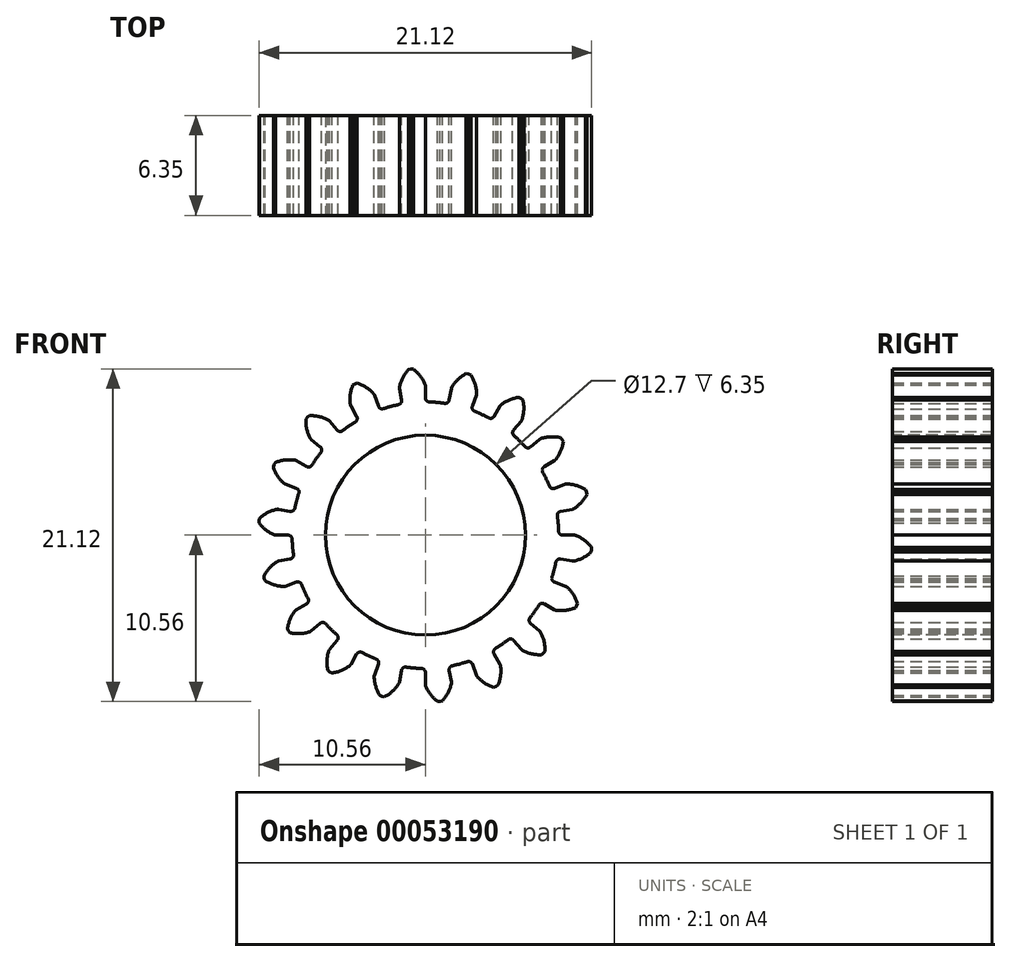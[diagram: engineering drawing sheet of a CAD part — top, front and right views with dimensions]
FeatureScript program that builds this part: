
annotation { "Feature Type Name" : "Feature", "Feature Type Description" : "" }
export const myFeature = defineFeature(function(context is Context, id is Id, definition is map)
    precondition{}
    {
        {
            var Q0;
            Q0=qCreatedBy(makeId("Front.planeOp"),FACE);
            var sketch = newSketch(context, id + "F0", { "sketchPlane" : qUnion([Q0])});
            skArc(sketch, "E0", {"start": v(-1.71, 8.3) * mm, "mid": v(-2.31, 8.15) * mm, "end": v(-2.9, 7.96) * mm});
            skLineSegment(sketch, "E1", {"start": v(0, 8.72) * mm, "end": v(0, 9.48) * mm});
            skArc(sketch, "E2", {"start": v(-0.02, 9.57) * mm, "mid": v(-0.33, 10.11) * mm, "end": v(-0.77, 10.56) * mm});
            skLineSegment(sketch, "E3", {"start": v(-0.77, 10.56) * mm, "end": v(-0.92, 10.56) * mm});
            skArc(sketch, "E4.MirrorCS", {"start": v(-1.64, 9.43) * mm, "mid": v(-1.43, 10.02) * mm, "end": v(-1.08, 10.53) * mm});
            skLineSegment(sketch, "E5.MirrorCS", {"start": v(-1.08, 10.53) * mm, "end": v(-0.92, 10.56) * mm});
            skLineSegment(sketch, "E6.MirrorCS", {"start": v(-1.51, 8.58) * mm, "end": v(-1.65, 9.33) * mm});
            skPoint(sketch, "E7.visualSharp", {"position": v(0, 9.53) * mm});
            skArc(sketch, "E7.filletArc", {"start": v(0, 9.48) * mm, "mid": v(0, 9.53) * mm, "end": v(-0.02, 9.57) * mm});
            skPoint(sketch, "E8.visualSharp", {"position": v(-1.65, 9.38) * mm});
            skArc(sketch, "E8.filletArc", {"start": v(-1.64, 9.43) * mm, "mid": v(-1.65, 9.38) * mm, "end": v(-1.65, 9.33) * mm});
            skPoint(sketch, "E9.visualSharp", {"position": v(0, 8.47) * mm});
            skArc(sketch, "E9.filletArc", {"start": v(0, 8.72) * mm, "mid": v(0.07, 8.54) * mm, "end": v(0.25, 8.46) * mm});
            skPoint(sketch, "E10.visualSharp", {"position": v(-1.47, 8.34) * mm});
            skArc(sketch, "E10.filletArc", {"start": v(-1.71, 8.3) * mm, "mid": v(-1.55, 8.4) * mm, "end": v(-1.51, 8.58) * mm});
            skLineSegment(sketch, "E11.1.0", {"start": v(-4.36, 7.55) * mm, "end": v(-4.74, 8.2) * mm});
            skLineSegment(sketch, "E11.1.1", {"start": v(-2.98, 8.2) * mm, "end": v(-3.24, 8.9) * mm});
            skPoint(sketch, "E11.1.2", {"position": v(-4.23, 7.33) * mm});
            skArc(sketch, "E11.1.3", {"start": v(-3.3, 8.99) * mm, "mid": v(-3.77, 9.4) * mm, "end": v(-4.33, 9.66) * mm});
            skArc(sketch, "E11.1.4", {"start": v(-2.98, 8.2) * mm, "mid": v(-2.85, 8.05) * mm, "end": v(-2.66, 8.04) * mm});
            skArc(sketch, "E11.1.5", {"start": v(-4.77, 8.3) * mm, "mid": v(-4.77, 8.92) * mm, "end": v(-4.61, 9.53) * mm});
            skPoint(sketch, "E11.1.6", {"position": v(-3.26, 8.95) * mm});
            skPoint(sketch, "E11.1.7", {"position": v(-4.76, 8.25) * mm});
            skPoint(sketch, "E11.1.8", {"position": v(-2.9, 7.96) * mm});
            skArc(sketch, "E11.1.9", {"start": v(-4.45, 7.2) * mm, "mid": v(-4.33, 7.36) * mm, "end": v(-4.36, 7.55) * mm});
            skLineSegment(sketch, "E11.1.10", {"start": v(-4.61, 9.53) * mm, "end": v(-4.48, 9.6) * mm});
            skLineSegment(sketch, "E11.1.11", {"start": v(-4.33, 9.66) * mm, "end": v(-4.48, 9.6) * mm});
            skArc(sketch, "E11.1.12", {"start": v(-4.77, 8.3) * mm, "mid": v(-4.76, 8.25) * mm, "end": v(-4.74, 8.2) * mm});
            skArc(sketch, "E11.1.13", {"start": v(-3.24, 8.9) * mm, "mid": v(-3.26, 8.95) * mm, "end": v(-3.3, 8.99) * mm});
            skLineSegment(sketch, "E11.2.0", {"start": v(-6.68, 5.6) * mm, "end": v(-7.26, 6.1) * mm});
            skLineSegment(sketch, "E11.2.1", {"start": v(-5.6, 6.68) * mm, "end": v(-6.1, 7.26) * mm});
            skPoint(sketch, "E11.2.2", {"position": v(-6.49, 5.44) * mm});
            skArc(sketch, "E11.2.3", {"start": v(-6.17, 7.32) * mm, "mid": v(-6.75, 7.54) * mm, "end": v(-7.37, 7.6) * mm});
            skArc(sketch, "E11.2.4", {"start": v(-5.6, 6.68) * mm, "mid": v(-5.43, 6.59) * mm, "end": v(-5.25, 6.64) * mm});
            skArc(sketch, "E11.2.5", {"start": v(-7.32, 6.17) * mm, "mid": v(-7.54, 6.75) * mm, "end": v(-7.6, 7.37) * mm});
            skPoint(sketch, "E11.2.6", {"position": v(-6.12, 7.3) * mm});
            skPoint(sketch, "E11.2.7", {"position": v(-7.3, 6.12) * mm});
            skPoint(sketch, "E11.2.8", {"position": v(-5.44, 6.49) * mm});
            skArc(sketch, "E11.2.9", {"start": v(-6.64, 5.25) * mm, "mid": v(-6.59, 5.43) * mm, "end": v(-6.68, 5.6) * mm});
            skLineSegment(sketch, "E11.2.10", {"start": v(-7.6, 7.37) * mm, "end": v(-7.5, 7.5) * mm});
            skLineSegment(sketch, "E11.2.11", {"start": v(-7.37, 7.6) * mm, "end": v(-7.5, 7.5) * mm});
            skArc(sketch, "E11.2.12", {"start": v(-7.32, 6.17) * mm, "mid": v(-7.3, 6.13) * mm, "end": v(-7.26, 6.1) * mm});
            skArc(sketch, "E11.2.13", {"start": v(-6.1, 7.26) * mm, "mid": v(-6.13, 7.3) * mm, "end": v(-6.17, 7.32) * mm});
            skLineSegment(sketch, "E11.3.0", {"start": v(-8.2, 2.98) * mm, "end": v(-8.9, 3.24) * mm});
            skLineSegment(sketch, "E11.3.1", {"start": v(-7.55, 4.36) * mm, "end": v(-8.2, 4.74) * mm});
            skPoint(sketch, "E11.3.2", {"position": v(-7.96, 2.9) * mm});
            skArc(sketch, "E11.3.3", {"start": v(-8.3, 4.77) * mm, "mid": v(-8.92, 4.77) * mm, "end": v(-9.53, 4.61) * mm});
            skArc(sketch, "E11.3.4", {"start": v(-7.55, 4.36) * mm, "mid": v(-7.36, 4.33) * mm, "end": v(-7.2, 4.45) * mm});
            skArc(sketch, "E11.3.5", {"start": v(-8.99, 3.3) * mm, "mid": v(-9.4, 3.77) * mm, "end": v(-9.66, 4.33) * mm});
            skPoint(sketch, "E11.3.6", {"position": v(-8.25, 4.76) * mm});
            skPoint(sketch, "E11.3.7", {"position": v(-8.95, 3.26) * mm});
            skPoint(sketch, "E11.3.8", {"position": v(-7.33, 4.23) * mm});
            skArc(sketch, "E11.3.9", {"start": v(-8.04, 2.66) * mm, "mid": v(-8.05, 2.85) * mm, "end": v(-8.2, 2.98) * mm});
            skLineSegment(sketch, "E11.3.10", {"start": v(-9.66, 4.33) * mm, "end": v(-9.6, 4.48) * mm});
            skLineSegment(sketch, "E11.3.11", {"start": v(-9.53, 4.61) * mm, "end": v(-9.6, 4.48) * mm});
            skArc(sketch, "E11.3.12", {"start": v(-8.99, 3.3) * mm, "mid": v(-8.95, 3.26) * mm, "end": v(-8.9, 3.24) * mm});
            skArc(sketch, "E11.3.13", {"start": v(-8.2, 4.74) * mm, "mid": v(-8.25, 4.76) * mm, "end": v(-8.3, 4.77) * mm});
            skLineSegment(sketch, "E11.4.0", {"start": v(-8.72, 0) * mm, "end": v(-9.48, 0) * mm});
            skLineSegment(sketch, "E11.4.1", {"start": v(-8.58, 1.51) * mm, "end": v(-9.33, 1.65) * mm});
            skPoint(sketch, "E11.4.2", {"position": v(-8.47, 0) * mm});
            skArc(sketch, "E11.4.3", {"start": v(-9.43, 1.64) * mm, "mid": v(-10.02, 1.43) * mm, "end": v(-10.53, 1.08) * mm});
            skArc(sketch, "E11.4.4", {"start": v(-8.58, 1.51) * mm, "mid": v(-8.4, 1.55) * mm, "end": v(-8.3, 1.71) * mm});
            skArc(sketch, "E11.4.5", {"start": v(-9.57, 0.02) * mm, "mid": v(-10.11, 0.33) * mm, "end": v(-10.56, 0.77) * mm});
            skPoint(sketch, "E11.4.6", {"position": v(-9.38, 1.65) * mm});
            skPoint(sketch, "E11.4.7", {"position": v(-9.53, 0) * mm});
            skPoint(sketch, "E11.4.8", {"position": v(-8.34, 1.47) * mm});
            skArc(sketch, "E11.4.9", {"start": v(-8.46, -0.25) * mm, "mid": v(-8.54, -0.07) * mm, "end": v(-8.72, 0) * mm});
            skLineSegment(sketch, "E11.4.10", {"start": v(-10.56, 0.77) * mm, "end": v(-10.56, 0.92) * mm});
            skLineSegment(sketch, "E11.4.11", {"start": v(-10.53, 1.08) * mm, "end": v(-10.56, 0.92) * mm});
            skArc(sketch, "E11.4.12", {"start": v(-9.57, 0.02) * mm, "mid": v(-9.53, 0) * mm, "end": v(-9.48, 0) * mm});
            skArc(sketch, "E11.4.13", {"start": v(-9.33, 1.65) * mm, "mid": v(-9.38, 1.65) * mm, "end": v(-9.43, 1.64) * mm});
            skLineSegment(sketch, "E11.5.0", {"start": v(-8.2, -2.98) * mm, "end": v(-8.9, -3.24) * mm});
            skLineSegment(sketch, "E11.5.1", {"start": v(-8.58, -1.51) * mm, "end": v(-9.33, -1.65) * mm});
            skPoint(sketch, "E11.5.2", {"position": v(-7.96, -2.9) * mm});
            skArc(sketch, "E11.5.3", {"start": v(-9.42, -1.68) * mm, "mid": v(-9.9, -2.08) * mm, "end": v(-10.26, -2.59) * mm});
            skArc(sketch, "E11.5.4", {"start": v(-8.58, -1.51) * mm, "mid": v(-8.42, -1.41) * mm, "end": v(-8.38, -1.23) * mm});
            skArc(sketch, "E11.5.5", {"start": v(-9, -3.26) * mm, "mid": v(-9.62, -3.15) * mm, "end": v(-10.18, -2.89) * mm});
            skPoint(sketch, "E11.5.6", {"position": v(-9.38, -1.65) * mm});
            skPoint(sketch, "E11.5.7", {"position": v(-8.95, -3.26) * mm});
            skPoint(sketch, "E11.5.8", {"position": v(-8.34, -1.47) * mm});
            skArc(sketch, "E11.5.9", {"start": v(-7.87, -3.13) * mm, "mid": v(-8, -2.99) * mm, "end": v(-8.2, -2.98) * mm});
            skLineSegment(sketch, "E11.5.10", {"start": v(-10.18, -2.89) * mm, "end": v(-10.23, -2.74) * mm});
            skLineSegment(sketch, "E11.5.11", {"start": v(-10.26, -2.59) * mm, "end": v(-10.23, -2.74) * mm});
            skArc(sketch, "E11.5.12", {"start": v(-9, -3.26) * mm, "mid": v(-8.95, -3.25) * mm, "end": v(-8.9, -3.24) * mm});
            skArc(sketch, "E11.5.13", {"start": v(-9.33, -1.65) * mm, "mid": v(-9.38, -1.66) * mm, "end": v(-9.42, -1.68) * mm});
            skLineSegment(sketch, "E11.6.0", {"start": v(-6.68, -5.6) * mm, "end": v(-7.26, -6.1) * mm});
            skLineSegment(sketch, "E11.6.1", {"start": v(-7.55, -4.36) * mm, "end": v(-8.2, -4.74) * mm});
            skPoint(sketch, "E11.6.2", {"position": v(-6.49, -5.44) * mm});
            skArc(sketch, "E11.6.3", {"start": v(-8.28, -4.8) * mm, "mid": v(-8.6, -5.34) * mm, "end": v(-8.76, -5.94) * mm});
            skArc(sketch, "E11.6.4", {"start": v(-7.55, -4.36) * mm, "mid": v(-7.43, -4.2) * mm, "end": v(-7.45, -4.02) * mm});
            skArc(sketch, "E11.6.5", {"start": v(-7.35, -6.14) * mm, "mid": v(-7.96, -6.25) * mm, "end": v(-8.58, -6.2) * mm});
            skPoint(sketch, "E11.6.6", {"position": v(-8.25, -4.76) * mm});
            skPoint(sketch, "E11.6.7", {"position": v(-7.3, -6.12) * mm});
            skPoint(sketch, "E11.6.8", {"position": v(-7.33, -4.23) * mm});
            skArc(sketch, "E11.6.9", {"start": v(-6.32, -5.63) * mm, "mid": v(-6.5, -5.54) * mm, "end": v(-6.68, -5.6) * mm});
            skLineSegment(sketch, "E11.6.10", {"start": v(-8.58, -6.2) * mm, "end": v(-8.68, -6.08) * mm});
            skLineSegment(sketch, "E11.6.11", {"start": v(-8.76, -5.94) * mm, "end": v(-8.68, -6.08) * mm});
            skArc(sketch, "E11.6.12", {"start": v(-7.35, -6.14) * mm, "mid": v(-7.3, -6.12) * mm, "end": v(-7.26, -6.1) * mm});
            skArc(sketch, "E11.6.13", {"start": v(-8.2, -4.74) * mm, "mid": v(-8.25, -4.77) * mm, "end": v(-8.28, -4.8) * mm});
            skLineSegment(sketch, "E11.7.0", {"start": v(-4.36, -7.55) * mm, "end": v(-4.74, -8.2) * mm});
            skLineSegment(sketch, "E11.7.1", {"start": v(-5.6, -6.68) * mm, "end": v(-6.1, -7.26) * mm});
            skPoint(sketch, "E11.7.2", {"position": v(-4.23, -7.33) * mm});
            skArc(sketch, "E11.7.3", {"start": v(-6.14, -7.35) * mm, "mid": v(-6.25, -7.96) * mm, "end": v(-6.2, -8.58) * mm});
            skArc(sketch, "E11.7.4", {"start": v(-5.6, -6.68) * mm, "mid": v(-5.54, -6.5) * mm, "end": v(-5.63, -6.32) * mm});
            skArc(sketch, "E11.7.5", {"start": v(-4.8, -8.28) * mm, "mid": v(-5.34, -8.6) * mm, "end": v(-5.94, -8.76) * mm});
            skPoint(sketch, "E11.7.6", {"position": v(-6.12, -7.3) * mm});
            skPoint(sketch, "E11.7.7", {"position": v(-4.76, -8.25) * mm});
            skPoint(sketch, "E11.7.8", {"position": v(-5.44, -6.49) * mm});
            skArc(sketch, "E11.7.9", {"start": v(-4.02, -7.45) * mm, "mid": v(-4.2, -7.43) * mm, "end": v(-4.36, -7.55) * mm});
            skLineSegment(sketch, "E11.7.10", {"start": v(-5.94, -8.76) * mm, "end": v(-6.08, -8.68) * mm});
            skLineSegment(sketch, "E11.7.11", {"start": v(-6.2, -8.58) * mm, "end": v(-6.08, -8.68) * mm});
            skArc(sketch, "E11.7.12", {"start": v(-4.8, -8.28) * mm, "mid": v(-4.77, -8.25) * mm, "end": v(-4.74, -8.2) * mm});
            skArc(sketch, "E11.7.13", {"start": v(-6.1, -7.26) * mm, "mid": v(-6.12, -7.3) * mm, "end": v(-6.14, -7.35) * mm});
            skLineSegment(sketch, "E11.8.0", {"start": v(-1.51, -8.58) * mm, "end": v(-1.65, -9.33) * mm});
            skLineSegment(sketch, "E11.8.1", {"start": v(-2.98, -8.2) * mm, "end": v(-3.24, -8.9) * mm});
            skPoint(sketch, "E11.8.2", {"position": v(-1.47, -8.34) * mm});
            skArc(sketch, "E11.8.3", {"start": v(-3.26, -9) * mm, "mid": v(-3.15, -9.62) * mm, "end": v(-2.89, -10.18) * mm});
            skArc(sketch, "E11.8.4", {"start": v(-2.98, -8.2) * mm, "mid": v(-2.99, -8) * mm, "end": v(-3.13, -7.87) * mm});
            skArc(sketch, "E11.8.5", {"start": v(-1.68, -9.42) * mm, "mid": v(-2.08, -9.9) * mm, "end": v(-2.59, -10.26) * mm});
            skPoint(sketch, "E11.8.6", {"position": v(-3.26, -8.95) * mm});
            skPoint(sketch, "E11.8.7", {"position": v(-1.65, -9.38) * mm});
            skPoint(sketch, "E11.8.8", {"position": v(-2.9, -7.96) * mm});
            skArc(sketch, "E11.8.9", {"start": v(-1.23, -8.38) * mm, "mid": v(-1.41, -8.42) * mm, "end": v(-1.51, -8.58) * mm});
            skLineSegment(sketch, "E11.8.10", {"start": v(-2.59, -10.26) * mm, "end": v(-2.74, -10.23) * mm});
            skLineSegment(sketch, "E11.8.11", {"start": v(-2.89, -10.18) * mm, "end": v(-2.74, -10.23) * mm});
            skArc(sketch, "E11.8.12", {"start": v(-1.68, -9.42) * mm, "mid": v(-1.66, -9.38) * mm, "end": v(-1.65, -9.33) * mm});
            skArc(sketch, "E11.8.13", {"start": v(-3.24, -8.9) * mm, "mid": v(-3.25, -8.95) * mm, "end": v(-3.26, -9) * mm});
            skLineSegment(sketch, "E11.9.0", {"start": v(1.51, -8.58) * mm, "end": v(1.65, -9.33) * mm});
            skLineSegment(sketch, "E11.9.1", {"start": v(0, -8.72) * mm, "end": v(0, -9.48) * mm});
            skPoint(sketch, "E11.9.2", {"position": v(1.47, -8.34) * mm});
            skArc(sketch, "E11.9.3", {"start": v(0.02, -9.57) * mm, "mid": v(0.33, -10.11) * mm, "end": v(0.77, -10.56) * mm});
            skArc(sketch, "E11.9.4", {"start": v(0, -8.72) * mm, "mid": v(-0.07, -8.54) * mm, "end": v(-0.25, -8.46) * mm});
            skArc(sketch, "E11.9.5", {"start": v(1.64, -9.43) * mm, "mid": v(1.43, -10.02) * mm, "end": v(1.08, -10.53) * mm});
            skPoint(sketch, "E11.9.6", {"position": v(0, -9.53) * mm});
            skPoint(sketch, "E11.9.7", {"position": v(1.65, -9.38) * mm});
            skPoint(sketch, "E11.9.8", {"position": v(0, -8.47) * mm});
            skArc(sketch, "E11.9.9", {"start": v(1.71, -8.3) * mm, "mid": v(1.55, -8.4) * mm, "end": v(1.51, -8.58) * mm});
            skLineSegment(sketch, "E11.9.10", {"start": v(1.08, -10.53) * mm, "end": v(0.92, -10.56) * mm});
            skLineSegment(sketch, "E11.9.11", {"start": v(0.77, -10.56) * mm, "end": v(0.92, -10.56) * mm});
            skArc(sketch, "E11.9.12", {"start": v(1.64, -9.43) * mm, "mid": v(1.65, -9.38) * mm, "end": v(1.65, -9.33) * mm});
            skArc(sketch, "E11.9.13", {"start": v(0, -9.48) * mm, "mid": v(0, -9.53) * mm, "end": v(0.02, -9.57) * mm});
            skLineSegment(sketch, "E11.10.0", {"start": v(4.36, -7.55) * mm, "end": v(4.74, -8.2) * mm});
            skLineSegment(sketch, "E11.10.1", {"start": v(2.98, -8.2) * mm, "end": v(3.24, -8.9) * mm});
            skPoint(sketch, "E11.10.2", {"position": v(4.23, -7.33) * mm});
            skArc(sketch, "E11.10.3", {"start": v(3.3, -8.99) * mm, "mid": v(3.77, -9.4) * mm, "end": v(4.33, -9.66) * mm});
            skArc(sketch, "E11.10.4", {"start": v(2.98, -8.2) * mm, "mid": v(2.85, -8.05) * mm, "end": v(2.66, -8.04) * mm});
            skArc(sketch, "E11.10.5", {"start": v(4.77, -8.3) * mm, "mid": v(4.77, -8.92) * mm, "end": v(4.61, -9.53) * mm});
            skPoint(sketch, "E11.10.6", {"position": v(3.26, -8.95) * mm});
            skPoint(sketch, "E11.10.7", {"position": v(4.76, -8.25) * mm});
            skPoint(sketch, "E11.10.8", {"position": v(2.9, -7.96) * mm});
            skArc(sketch, "E11.10.9", {"start": v(4.45, -7.2) * mm, "mid": v(4.33, -7.36) * mm, "end": v(4.36, -7.55) * mm});
            skLineSegment(sketch, "E11.10.10", {"start": v(4.61, -9.53) * mm, "end": v(4.48, -9.6) * mm});
            skLineSegment(sketch, "E11.10.11", {"start": v(4.33, -9.66) * mm, "end": v(4.48, -9.6) * mm});
            skArc(sketch, "E11.10.12", {"start": v(4.77, -8.3) * mm, "mid": v(4.76, -8.25) * mm, "end": v(4.74, -8.2) * mm});
            skArc(sketch, "E11.10.13", {"start": v(3.24, -8.9) * mm, "mid": v(3.26, -8.95) * mm, "end": v(3.3, -8.99) * mm});
            skLineSegment(sketch, "E11.11.0", {"start": v(6.68, -5.6) * mm, "end": v(7.26, -6.1) * mm});
            skLineSegment(sketch, "E11.11.1", {"start": v(5.6, -6.68) * mm, "end": v(6.1, -7.26) * mm});
            skPoint(sketch, "E11.11.2", {"position": v(6.49, -5.44) * mm});
            skArc(sketch, "E11.11.3", {"start": v(6.17, -7.32) * mm, "mid": v(6.75, -7.54) * mm, "end": v(7.37, -7.6) * mm});
            skArc(sketch, "E11.11.4", {"start": v(5.6, -6.68) * mm, "mid": v(5.43, -6.59) * mm, "end": v(5.25, -6.64) * mm});
            skArc(sketch, "E11.11.5", {"start": v(7.32, -6.17) * mm, "mid": v(7.54, -6.75) * mm, "end": v(7.6, -7.37) * mm});
            skPoint(sketch, "E11.11.6", {"position": v(6.12, -7.3) * mm});
            skPoint(sketch, "E11.11.7", {"position": v(7.3, -6.12) * mm});
            skPoint(sketch, "E11.11.8", {"position": v(5.44, -6.49) * mm});
            skArc(sketch, "E11.11.9", {"start": v(6.64, -5.25) * mm, "mid": v(6.59, -5.43) * mm, "end": v(6.68, -5.6) * mm});
            skLineSegment(sketch, "E11.11.10", {"start": v(7.6, -7.37) * mm, "end": v(7.5, -7.5) * mm});
            skLineSegment(sketch, "E11.11.11", {"start": v(7.37, -7.6) * mm, "end": v(7.5, -7.5) * mm});
            skArc(sketch, "E11.11.12", {"start": v(7.32, -6.17) * mm, "mid": v(7.3, -6.13) * mm, "end": v(7.26, -6.1) * mm});
            skArc(sketch, "E11.11.13", {"start": v(6.1, -7.26) * mm, "mid": v(6.13, -7.3) * mm, "end": v(6.17, -7.32) * mm});
            skLineSegment(sketch, "E11.12.0", {"start": v(8.2, -2.98) * mm, "end": v(8.9, -3.24) * mm});
            skLineSegment(sketch, "E11.12.1", {"start": v(7.55, -4.36) * mm, "end": v(8.2, -4.74) * mm});
            skPoint(sketch, "E11.12.2", {"position": v(7.96, -2.9) * mm});
            skArc(sketch, "E11.12.3", {"start": v(8.3, -4.77) * mm, "mid": v(8.92, -4.77) * mm, "end": v(9.53, -4.61) * mm});
            skArc(sketch, "E11.12.4", {"start": v(7.55, -4.36) * mm, "mid": v(7.36, -4.33) * mm, "end": v(7.2, -4.45) * mm});
            skArc(sketch, "E11.12.5", {"start": v(8.99, -3.3) * mm, "mid": v(9.4, -3.77) * mm, "end": v(9.66, -4.33) * mm});
            skPoint(sketch, "E11.12.6", {"position": v(8.25, -4.76) * mm});
            skPoint(sketch, "E11.12.7", {"position": v(8.95, -3.26) * mm});
            skPoint(sketch, "E11.12.8", {"position": v(7.33, -4.23) * mm});
            skArc(sketch, "E11.12.9", {"start": v(8.04, -2.66) * mm, "mid": v(8.05, -2.85) * mm, "end": v(8.2, -2.98) * mm});
            skLineSegment(sketch, "E11.12.10", {"start": v(9.66, -4.33) * mm, "end": v(9.6, -4.48) * mm});
            skLineSegment(sketch, "E11.12.11", {"start": v(9.53, -4.61) * mm, "end": v(9.6, -4.48) * mm});
            skArc(sketch, "E11.12.12", {"start": v(8.99, -3.3) * mm, "mid": v(8.95, -3.26) * mm, "end": v(8.9, -3.24) * mm});
            skArc(sketch, "E11.12.13", {"start": v(8.2, -4.74) * mm, "mid": v(8.25, -4.76) * mm, "end": v(8.3, -4.77) * mm});
            skLineSegment(sketch, "E11.13.0", {"start": v(8.72, 0) * mm, "end": v(9.48, 0) * mm});
            skLineSegment(sketch, "E11.13.1", {"start": v(8.58, -1.51) * mm, "end": v(9.33, -1.65) * mm});
            skPoint(sketch, "E11.13.2", {"position": v(8.47, 0) * mm});
            skArc(sketch, "E11.13.3", {"start": v(9.43, -1.64) * mm, "mid": v(10.02, -1.43) * mm, "end": v(10.53, -1.08) * mm});
            skArc(sketch, "E11.13.4", {"start": v(8.58, -1.51) * mm, "mid": v(8.4, -1.55) * mm, "end": v(8.3, -1.71) * mm});
            skArc(sketch, "E11.13.5", {"start": v(9.57, -0.02) * mm, "mid": v(10.11, -0.33) * mm, "end": v(10.56, -0.77) * mm});
            skPoint(sketch, "E11.13.6", {"position": v(9.38, -1.65) * mm});
            skPoint(sketch, "E11.13.7", {"position": v(9.53, 0) * mm});
            skPoint(sketch, "E11.13.8", {"position": v(8.34, -1.47) * mm});
            skArc(sketch, "E11.13.9", {"start": v(8.46, 0.25) * mm, "mid": v(8.54, 0.07) * mm, "end": v(8.72, 0) * mm});
            skLineSegment(sketch, "E11.13.10", {"start": v(10.56, -0.77) * mm, "end": v(10.56, -0.92) * mm});
            skLineSegment(sketch, "E11.13.11", {"start": v(10.53, -1.08) * mm, "end": v(10.56, -0.92) * mm});
            skArc(sketch, "E11.13.12", {"start": v(9.57, -0.02) * mm, "mid": v(9.53, 0) * mm, "end": v(9.48, 0) * mm});
            skArc(sketch, "E11.13.13", {"start": v(9.33, -1.65) * mm, "mid": v(9.38, -1.65) * mm, "end": v(9.43, -1.64) * mm});
            skLineSegment(sketch, "E11.14.0", {"start": v(8.2, 2.98) * mm, "end": v(8.9, 3.24) * mm});
            skLineSegment(sketch, "E11.14.1", {"start": v(8.58, 1.51) * mm, "end": v(9.33, 1.65) * mm});
            skPoint(sketch, "E11.14.2", {"position": v(7.96, 2.9) * mm});
            skArc(sketch, "E11.14.3", {"start": v(9.42, 1.68) * mm, "mid": v(9.9, 2.08) * mm, "end": v(10.26, 2.59) * mm});
            skArc(sketch, "E11.14.4", {"start": v(8.58, 1.51) * mm, "mid": v(8.42, 1.41) * mm, "end": v(8.38, 1.23) * mm});
            skArc(sketch, "E11.14.5", {"start": v(9, 3.26) * mm, "mid": v(9.62, 3.15) * mm, "end": v(10.18, 2.89) * mm});
            skPoint(sketch, "E11.14.6", {"position": v(9.38, 1.65) * mm});
            skPoint(sketch, "E11.14.7", {"position": v(8.95, 3.26) * mm});
            skPoint(sketch, "E11.14.8", {"position": v(8.34, 1.47) * mm});
            skArc(sketch, "E11.14.9", {"start": v(7.87, 3.13) * mm, "mid": v(8, 2.99) * mm, "end": v(8.2, 2.98) * mm});
            skLineSegment(sketch, "E11.14.10", {"start": v(10.18, 2.89) * mm, "end": v(10.23, 2.74) * mm});
            skLineSegment(sketch, "E11.14.11", {"start": v(10.26, 2.59) * mm, "end": v(10.23, 2.74) * mm});
            skArc(sketch, "E11.14.12", {"start": v(9, 3.26) * mm, "mid": v(8.95, 3.25) * mm, "end": v(8.9, 3.24) * mm});
            skArc(sketch, "E11.14.13", {"start": v(9.33, 1.65) * mm, "mid": v(9.38, 1.66) * mm, "end": v(9.42, 1.68) * mm});
            skLineSegment(sketch, "E11.15.0", {"start": v(6.68, 5.6) * mm, "end": v(7.26, 6.1) * mm});
            skLineSegment(sketch, "E11.15.1", {"start": v(7.55, 4.36) * mm, "end": v(8.2, 4.74) * mm});
            skPoint(sketch, "E11.15.2", {"position": v(6.49, 5.44) * mm});
            skArc(sketch, "E11.15.3", {"start": v(8.28, 4.8) * mm, "mid": v(8.6, 5.34) * mm, "end": v(8.76, 5.94) * mm});
            skArc(sketch, "E11.15.4", {"start": v(7.55, 4.36) * mm, "mid": v(7.43, 4.2) * mm, "end": v(7.45, 4.02) * mm});
            skArc(sketch, "E11.15.5", {"start": v(7.35, 6.14) * mm, "mid": v(7.96, 6.25) * mm, "end": v(8.58, 6.2) * mm});
            skPoint(sketch, "E11.15.6", {"position": v(8.25, 4.76) * mm});
            skPoint(sketch, "E11.15.7", {"position": v(7.3, 6.12) * mm});
            skPoint(sketch, "E11.15.8", {"position": v(7.33, 4.23) * mm});
            skArc(sketch, "E11.15.9", {"start": v(6.32, 5.63) * mm, "mid": v(6.5, 5.54) * mm, "end": v(6.68, 5.6) * mm});
            skLineSegment(sketch, "E11.15.10", {"start": v(8.58, 6.2) * mm, "end": v(8.68, 6.08) * mm});
            skLineSegment(sketch, "E11.15.11", {"start": v(8.76, 5.94) * mm, "end": v(8.68, 6.08) * mm});
            skArc(sketch, "E11.15.12", {"start": v(7.35, 6.14) * mm, "mid": v(7.3, 6.12) * mm, "end": v(7.26, 6.1) * mm});
            skArc(sketch, "E11.15.13", {"start": v(8.2, 4.74) * mm, "mid": v(8.25, 4.77) * mm, "end": v(8.28, 4.8) * mm});
            skLineSegment(sketch, "E11.16.0", {"start": v(4.36, 7.55) * mm, "end": v(4.74, 8.2) * mm});
            skLineSegment(sketch, "E11.16.1", {"start": v(5.6, 6.68) * mm, "end": v(6.1, 7.26) * mm});
            skPoint(sketch, "E11.16.2", {"position": v(4.23, 7.33) * mm});
            skArc(sketch, "E11.16.3", {"start": v(6.14, 7.35) * mm, "mid": v(6.25, 7.96) * mm, "end": v(6.2, 8.58) * mm});
            skArc(sketch, "E11.16.4", {"start": v(5.6, 6.68) * mm, "mid": v(5.54, 6.5) * mm, "end": v(5.63, 6.32) * mm});
            skArc(sketch, "E11.16.5", {"start": v(4.8, 8.28) * mm, "mid": v(5.34, 8.6) * mm, "end": v(5.94, 8.76) * mm});
            skPoint(sketch, "E11.16.6", {"position": v(6.12, 7.3) * mm});
            skPoint(sketch, "E11.16.7", {"position": v(4.76, 8.25) * mm});
            skPoint(sketch, "E11.16.8", {"position": v(5.44, 6.49) * mm});
            skArc(sketch, "E11.16.9", {"start": v(4.02, 7.45) * mm, "mid": v(4.2, 7.43) * mm, "end": v(4.36, 7.55) * mm});
            skLineSegment(sketch, "E11.16.10", {"start": v(5.94, 8.76) * mm, "end": v(6.08, 8.68) * mm});
            skLineSegment(sketch, "E11.16.11", {"start": v(6.2, 8.58) * mm, "end": v(6.08, 8.68) * mm});
            skArc(sketch, "E11.16.12", {"start": v(4.8, 8.28) * mm, "mid": v(4.77, 8.25) * mm, "end": v(4.74, 8.2) * mm});
            skArc(sketch, "E11.16.13", {"start": v(6.1, 7.26) * mm, "mid": v(6.12, 7.3) * mm, "end": v(6.14, 7.35) * mm});
            skLineSegment(sketch, "E11.17.0", {"start": v(1.51, 8.58) * mm, "end": v(1.65, 9.33) * mm});
            skLineSegment(sketch, "E11.17.1", {"start": v(2.98, 8.2) * mm, "end": v(3.24, 8.9) * mm});
            skPoint(sketch, "E11.17.2", {"position": v(1.47, 8.34) * mm});
            skArc(sketch, "E11.17.3", {"start": v(3.26, 9) * mm, "mid": v(3.15, 9.62) * mm, "end": v(2.89, 10.18) * mm});
            skArc(sketch, "E11.17.4", {"start": v(2.98, 8.2) * mm, "mid": v(2.99, 8) * mm, "end": v(3.13, 7.87) * mm});
            skArc(sketch, "E11.17.5", {"start": v(1.68, 9.42) * mm, "mid": v(2.08, 9.9) * mm, "end": v(2.59, 10.26) * mm});
            skPoint(sketch, "E11.17.6", {"position": v(3.26, 8.95) * mm});
            skPoint(sketch, "E11.17.7", {"position": v(1.65, 9.38) * mm});
            skPoint(sketch, "E11.17.8", {"position": v(2.9, 7.96) * mm});
            skArc(sketch, "E11.17.9", {"start": v(1.23, 8.38) * mm, "mid": v(1.41, 8.42) * mm, "end": v(1.51, 8.58) * mm});
            skLineSegment(sketch, "E11.17.10", {"start": v(2.59, 10.26) * mm, "end": v(2.74, 10.23) * mm});
            skLineSegment(sketch, "E11.17.11", {"start": v(2.89, 10.18) * mm, "end": v(2.74, 10.23) * mm});
            skArc(sketch, "E11.17.12", {"start": v(1.68, 9.42) * mm, "mid": v(1.66, 9.38) * mm, "end": v(1.65, 9.33) * mm});
            skArc(sketch, "E11.17.13", {"start": v(3.24, 8.9) * mm, "mid": v(3.25, 8.95) * mm, "end": v(3.26, 9) * mm});
            skArc(sketch, "E12.trimOffspring", {"start": v(1.23, 8.38) * mm, "mid": v(0.74, 8.43) * mm, "end": v(0.25, 8.46) * mm});
            skArc(sketch, "E13.trimOffspring", {"start": v(4.02, 7.45) * mm, "mid": v(3.58, 7.67) * mm, "end": v(3.13, 7.87) * mm});
            skArc(sketch, "E14.trimOffspring", {"start": v(6.49, 5.44) * mm, "mid": v(5.99, 5.99) * mm, "end": v(5.44, 6.49) * mm});
            skArc(sketch, "E15.trimOffspring", {"start": v(7.96, 2.9) * mm, "mid": v(7.67, 3.58) * mm, "end": v(7.33, 4.23) * mm});
            skArc(sketch, "E16.trimOffspring", {"start": v(8.47, 0) * mm, "mid": v(8.43, 0.74) * mm, "end": v(8.34, 1.47) * mm});
            skArc(sketch, "E17.trimOffspring", {"start": v(7.96, -2.9) * mm, "mid": v(8.18, -2.2) * mm, "end": v(8.34, -1.47) * mm});
            skArc(sketch, "E18.trimOffspring", {"start": v(6.49, -5.44) * mm, "mid": v(6.94, -4.86) * mm, "end": v(7.33, -4.23) * mm});
            skArc(sketch, "E19.trimOffspring", {"start": v(4.23, -7.33) * mm, "mid": v(4.86, -6.94) * mm, "end": v(5.44, -6.49) * mm});
            skArc(sketch, "E20.trimOffspring", {"start": v(1.47, -8.34) * mm, "mid": v(2.2, -8.18) * mm, "end": v(2.9, -7.96) * mm});
            skArc(sketch, "E21.trimOffspring", {"start": v(-1.47, -8.34) * mm, "mid": v(-0.74, -8.43) * mm, "end": v(0, -8.47) * mm});
            skArc(sketch, "E22.trimOffspring", {"start": v(-4.23, -7.33) * mm, "mid": v(-3.58, -7.67) * mm, "end": v(-2.9, -7.96) * mm});
            skArc(sketch, "E23.trimOffspring", {"start": v(-6.49, -5.44) * mm, "mid": v(-6.07, -5.9) * mm, "end": v(-5.63, -6.32) * mm});
            skArc(sketch, "E24.trimOffspring", {"start": v(-7.96, -2.9) * mm, "mid": v(-7.67, -3.58) * mm, "end": v(-7.33, -4.23) * mm});
            skArc(sketch, "E25.trimOffspring", {"start": v(-8.47, 0) * mm, "mid": v(-8.43, -0.74) * mm, "end": v(-8.34, -1.47) * mm});
            skArc(sketch, "E26.trimOffspring", {"start": v(-7.96, 2.9) * mm, "mid": v(-8.18, 2.2) * mm, "end": v(-8.34, 1.47) * mm});
            skArc(sketch, "E27.trimOffspring", {"start": v(-6.49, 5.44) * mm, "mid": v(-6.94, 4.86) * mm, "end": v(-7.33, 4.23) * mm});
            skArc(sketch, "E28.trimOffspring", {"start": v(-4.23, 7.33) * mm, "mid": v(-4.86, 6.94) * mm, "end": v(-5.44, 6.49) * mm});
            skSolve(sketch);
        }
        {
            var Q0;
            Q0=makeQuery(id+"F0.imprint","IMPRINT",FACE,{"disambiguationData":[TD([[makeQuery(id+"F0.imprint","IMPRINT",EDGE,{"derivedFrom":sQuery(id+"F0.wireOp",EDGE,"E1")}),1.0]])]});
            extrude(context, id + "F1", {"entities" : qUnion([Q0]), "depth" : 6.35 * mm});
        }
        {
            var Q0;
            Q0=makeQuery(id+"F1.opExtrude","CAP_FACE",FACE,{"disambiguationData":[OSD([sQuery(id+"F0.wireOp",EDGE,"E0"),sQuery(id+"F0.wireOp",EDGE,"E1"),sQuery(id+"F0.wireOp",EDGE,"E2"),sQuery(id+"F0.wireOp",EDGE,"E3"),sQuery(id+"F0.wireOp",EDGE,"E4.MirrorCS"),sQuery(id+"F0.wireOp",EDGE,"E5.MirrorCS"),sQuery(id+"F0.wireOp",EDGE,"E6.MirrorCS"),sQuery(id+"F0.wireOp",EDGE,"E7.filletArc"),sQuery(id+"F0.wireOp",EDGE,"E8.filletArc"),sQuery(id+"F0.wireOp",EDGE,"E9.filletArc"),sQuery(id+"F0.wireOp",EDGE,"E10.filletArc"),sQuery(id+"F0.wireOp",EDGE,"E11.1.0"),sQuery(id+"F0.wireOp",EDGE,"E11.1.1"),sQuery(id+"F0.wireOp",EDGE,"E11.1.3"),sQuery(id+"F0.wireOp",EDGE,"E11.1.4"),sQuery(id+"F0.wireOp",EDGE,"E11.1.5"),sQuery(id+"F0.wireOp",EDGE,"E11.1.9"),sQuery(id+"F0.wireOp",EDGE,"E11.1.10"),sQuery(id+"F0.wireOp",EDGE,"E11.1.11"),sQuery(id+"F0.wireOp",EDGE,"E11.1.12"),sQuery(id+"F0.wireOp",EDGE,"E11.1.13"),sQuery(id+"F0.wireOp",EDGE,"E11.2.0"),sQuery(id+"F0.wireOp",EDGE,"E11.2.1"),sQuery(id+"F0.wireOp",EDGE,"E11.2.3"),sQuery(id+"F0.wireOp",EDGE,"E11.2.4"),sQuery(id+"F0.wireOp",EDGE,"E11.2.5"),sQuery(id+"F0.wireOp",EDGE,"E11.2.9"),sQuery(id+"F0.wireOp",EDGE,"E11.2.10"),sQuery(id+"F0.wireOp",EDGE,"E11.2.11"),sQuery(id+"F0.wireOp",EDGE,"E11.2.12"),sQuery(id+"F0.wireOp",EDGE,"E11.2.13"),sQuery(id+"F0.wireOp",EDGE,"E11.3.0"),sQuery(id+"F0.wireOp",EDGE,"E11.3.1"),sQuery(id+"F0.wireOp",EDGE,"E11.3.3"),sQuery(id+"F0.wireOp",EDGE,"E11.3.4"),sQuery(id+"F0.wireOp",EDGE,"E11.3.5"),sQuery(id+"F0.wireOp",EDGE,"E11.3.9"),sQuery(id+"F0.wireOp",EDGE,"E11.3.10"),sQuery(id+"F0.wireOp",EDGE,"E11.3.11"),sQuery(id+"F0.wireOp",EDGE,"E11.3.12"),sQuery(id+"F0.wireOp",EDGE,"E11.3.13"),sQuery(id+"F0.wireOp",EDGE,"E11.4.0"),sQuery(id+"F0.wireOp",EDGE,"E11.4.1"),sQuery(id+"F0.wireOp",EDGE,"E11.4.3"),sQuery(id+"F0.wireOp",EDGE,"E11.4.4"),sQuery(id+"F0.wireOp",EDGE,"E11.4.5"),sQuery(id+"F0.wireOp",EDGE,"E11.4.9"),sQuery(id+"F0.wireOp",EDGE,"E11.4.10"),sQuery(id+"F0.wireOp",EDGE,"E11.4.11"),sQuery(id+"F0.wireOp",EDGE,"E11.4.12"),sQuery(id+"F0.wireOp",EDGE,"E11.4.13"),sQuery(id+"F0.wireOp",EDGE,"E11.5.0"),sQuery(id+"F0.wireOp",EDGE,"E11.5.1"),sQuery(id+"F0.wireOp",EDGE,"E11.5.3"),sQuery(id+"F0.wireOp",EDGE,"E11.5.4"),sQuery(id+"F0.wireOp",EDGE,"E11.5.5"),sQuery(id+"F0.wireOp",EDGE,"E11.5.9"),sQuery(id+"F0.wireOp",EDGE,"E11.5.10"),sQuery(id+"F0.wireOp",EDGE,"E11.5.11"),sQuery(id+"F0.wireOp",EDGE,"E11.5.12"),sQuery(id+"F0.wireOp",EDGE,"E11.5.13"),sQuery(id+"F0.wireOp",EDGE,"E11.6.0"),sQuery(id+"F0.wireOp",EDGE,"E11.6.1"),sQuery(id+"F0.wireOp",EDGE,"E11.6.3"),sQuery(id+"F0.wireOp",EDGE,"E11.6.4"),sQuery(id+"F0.wireOp",EDGE,"E11.6.5"),sQuery(id+"F0.wireOp",EDGE,"E11.6.9"),sQuery(id+"F0.wireOp",EDGE,"E11.6.10"),sQuery(id+"F0.wireOp",EDGE,"E11.6.11"),sQuery(id+"F0.wireOp",EDGE,"E11.6.12"),sQuery(id+"F0.wireOp",EDGE,"E11.6.13"),sQuery(id+"F0.wireOp",EDGE,"E11.7.0"),sQuery(id+"F0.wireOp",EDGE,"E11.7.1"),sQuery(id+"F0.wireOp",EDGE,"E11.7.3"),sQuery(id+"F0.wireOp",EDGE,"E11.7.4"),sQuery(id+"F0.wireOp",EDGE,"E11.7.5"),sQuery(id+"F0.wireOp",EDGE,"E11.7.9"),sQuery(id+"F0.wireOp",EDGE,"E11.7.10"),sQuery(id+"F0.wireOp",EDGE,"E11.7.11"),sQuery(id+"F0.wireOp",EDGE,"E11.7.12"),sQuery(id+"F0.wireOp",EDGE,"E11.7.13"),sQuery(id+"F0.wireOp",EDGE,"E11.8.0"),sQuery(id+"F0.wireOp",EDGE,"E11.8.1"),sQuery(id+"F0.wireOp",EDGE,"E11.8.3"),sQuery(id+"F0.wireOp",EDGE,"E11.8.4"),sQuery(id+"F0.wireOp",EDGE,"E11.8.5"),sQuery(id+"F0.wireOp",EDGE,"E11.8.9"),sQuery(id+"F0.wireOp",EDGE,"E11.8.10"),sQuery(id+"F0.wireOp",EDGE,"E11.8.11"),sQuery(id+"F0.wireOp",EDGE,"E11.8.12"),sQuery(id+"F0.wireOp",EDGE,"E11.8.13"),sQuery(id+"F0.wireOp",EDGE,"E11.9.0"),sQuery(id+"F0.wireOp",EDGE,"E11.9.1"),sQuery(id+"F0.wireOp",EDGE,"E11.9.3"),sQuery(id+"F0.wireOp",EDGE,"E11.9.4"),sQuery(id+"F0.wireOp",EDGE,"E11.9.5"),sQuery(id+"F0.wireOp",EDGE,"E11.9.9"),sQuery(id+"F0.wireOp",EDGE,"E11.9.10"),sQuery(id+"F0.wireOp",EDGE,"E11.9.11"),sQuery(id+"F0.wireOp",EDGE,"E11.9.12"),sQuery(id+"F0.wireOp",EDGE,"E11.9.13"),sQuery(id+"F0.wireOp",EDGE,"E11.10.0"),sQuery(id+"F0.wireOp",EDGE,"E11.10.1"),sQuery(id+"F0.wireOp",EDGE,"E11.10.3"),sQuery(id+"F0.wireOp",EDGE,"E11.10.4"),sQuery(id+"F0.wireOp",EDGE,"E11.10.5"),sQuery(id+"F0.wireOp",EDGE,"E11.10.9"),sQuery(id+"F0.wireOp",EDGE,"E11.10.10"),sQuery(id+"F0.wireOp",EDGE,"E11.10.11"),sQuery(id+"F0.wireOp",EDGE,"E11.10.12"),sQuery(id+"F0.wireOp",EDGE,"E11.10.13"),sQuery(id+"F0.wireOp",EDGE,"E11.11.0"),sQuery(id+"F0.wireOp",EDGE,"E11.11.1"),sQuery(id+"F0.wireOp",EDGE,"E11.11.3"),sQuery(id+"F0.wireOp",EDGE,"E11.11.4"),sQuery(id+"F0.wireOp",EDGE,"E11.11.5"),sQuery(id+"F0.wireOp",EDGE,"E11.11.9"),sQuery(id+"F0.wireOp",EDGE,"E11.11.10"),sQuery(id+"F0.wireOp",EDGE,"E11.11.11"),sQuery(id+"F0.wireOp",EDGE,"E11.11.12"),sQuery(id+"F0.wireOp",EDGE,"E11.11.13"),sQuery(id+"F0.wireOp",EDGE,"E11.12.0"),sQuery(id+"F0.wireOp",EDGE,"E11.12.1"),sQuery(id+"F0.wireOp",EDGE,"E11.12.3"),sQuery(id+"F0.wireOp",EDGE,"E11.12.4"),sQuery(id+"F0.wireOp",EDGE,"E11.12.5"),sQuery(id+"F0.wireOp",EDGE,"E11.12.9"),sQuery(id+"F0.wireOp",EDGE,"E11.12.10"),sQuery(id+"F0.wireOp",EDGE,"E11.12.11"),sQuery(id+"F0.wireOp",EDGE,"E11.12.12"),sQuery(id+"F0.wireOp",EDGE,"E11.12.13"),sQuery(id+"F0.wireOp",EDGE,"E11.13.0"),sQuery(id+"F0.wireOp",EDGE,"E11.13.1"),sQuery(id+"F0.wireOp",EDGE,"E11.13.3"),sQuery(id+"F0.wireOp",EDGE,"E11.13.4"),sQuery(id+"F0.wireOp",EDGE,"E11.13.5"),sQuery(id+"F0.wireOp",EDGE,"E11.13.9"),sQuery(id+"F0.wireOp",EDGE,"E11.13.10"),sQuery(id+"F0.wireOp",EDGE,"E11.13.11"),sQuery(id+"F0.wireOp",EDGE,"E11.13.12"),sQuery(id+"F0.wireOp",EDGE,"E11.13.13"),sQuery(id+"F0.wireOp",EDGE,"E11.14.0"),sQuery(id+"F0.wireOp",EDGE,"E11.14.1"),sQuery(id+"F0.wireOp",EDGE,"E11.14.3"),sQuery(id+"F0.wireOp",EDGE,"E11.14.4"),sQuery(id+"F0.wireOp",EDGE,"E11.14.5"),sQuery(id+"F0.wireOp",EDGE,"E11.14.9"),sQuery(id+"F0.wireOp",EDGE,"E11.14.10"),sQuery(id+"F0.wireOp",EDGE,"E11.14.11"),sQuery(id+"F0.wireOp",EDGE,"E11.14.12"),sQuery(id+"F0.wireOp",EDGE,"E11.14.13"),sQuery(id+"F0.wireOp",EDGE,"E11.15.0"),sQuery(id+"F0.wireOp",EDGE,"E11.15.1"),sQuery(id+"F0.wireOp",EDGE,"E11.15.3"),sQuery(id+"F0.wireOp",EDGE,"E11.15.4"),sQuery(id+"F0.wireOp",EDGE,"E11.15.5"),sQuery(id+"F0.wireOp",EDGE,"E11.15.9"),sQuery(id+"F0.wireOp",EDGE,"E11.15.10"),sQuery(id+"F0.wireOp",EDGE,"E11.15.11"),sQuery(id+"F0.wireOp",EDGE,"E11.15.12"),sQuery(id+"F0.wireOp",EDGE,"E11.15.13"),sQuery(id+"F0.wireOp",EDGE,"E11.16.0"),sQuery(id+"F0.wireOp",EDGE,"E11.16.1"),sQuery(id+"F0.wireOp",EDGE,"E11.16.3"),sQuery(id+"F0.wireOp",EDGE,"E11.16.4"),sQuery(id+"F0.wireOp",EDGE,"E11.16.5"),sQuery(id+"F0.wireOp",EDGE,"E11.16.9"),sQuery(id+"F0.wireOp",EDGE,"E11.16.10"),sQuery(id+"F0.wireOp",EDGE,"E11.16.11"),sQuery(id+"F0.wireOp",EDGE,"E11.16.12"),sQuery(id+"F0.wireOp",EDGE,"E11.16.13"),sQuery(id+"F0.wireOp",EDGE,"E11.17.0"),sQuery(id+"F0.wireOp",EDGE,"E11.17.1"),sQuery(id+"F0.wireOp",EDGE,"E11.17.3"),sQuery(id+"F0.wireOp",EDGE,"E11.17.4"),sQuery(id+"F0.wireOp",EDGE,"E11.17.5"),sQuery(id+"F0.wireOp",EDGE,"E11.17.9"),sQuery(id+"F0.wireOp",EDGE,"E11.17.10"),sQuery(id+"F0.wireOp",EDGE,"E11.17.11"),sQuery(id+"F0.wireOp",EDGE,"E11.17.12"),sQuery(id+"F0.wireOp",EDGE,"E11.17.13"),sQuery(id+"F0.wireOp",EDGE,"E12.trimOffspring"),sQuery(id+"F0.wireOp",EDGE,"E13.trimOffspring"),sQuery(id+"F0.wireOp",EDGE,"E14.trimOffspring"),sQuery(id+"F0.wireOp",EDGE,"E15.trimOffspring"),sQuery(id+"F0.wireOp",EDGE,"E16.trimOffspring"),sQuery(id+"F0.wireOp",EDGE,"E17.trimOffspring"),sQuery(id+"F0.wireOp",EDGE,"E18.trimOffspring"),sQuery(id+"F0.wireOp",EDGE,"E19.trimOffspring"),sQuery(id+"F0.wireOp",EDGE,"E20.trimOffspring"),sQuery(id+"F0.wireOp",EDGE,"E21.trimOffspring"),sQuery(id+"F0.wireOp",EDGE,"E22.trimOffspring"),sQuery(id+"F0.wireOp",EDGE,"E23.trimOffspring"),sQuery(id+"F0.wireOp",EDGE,"E24.trimOffspring"),sQuery(id+"F0.wireOp",EDGE,"E25.trimOffspring"),sQuery(id+"F0.wireOp",EDGE,"E26.trimOffspring"),sQuery(id+"F0.wireOp",EDGE,"E27.trimOffspring"),sQuery(id+"F0.wireOp",EDGE,"E28.trimOffspring")])],"isStart":false});
            var sketch = newSketch(context, id + "F2", { "sketchPlane" : qUnion([Q0])});
            skCircle(sketch, "E29", {"center": v(0, 0) * mm, "radius": 6.35 * mm});
            skSolve(sketch);
        }
        {
            var Q0;
            Q0=makeQuery(id+"F2.imprint","IMPRINT",FACE,{"disambiguationData":[TD([[makeQuery(id+"F2.imprint","IMPRINT",EDGE,{"derivedFrom":sQuery(id+"F2.wireOp",EDGE,"E29")}),1.0]])]});
            extrude(context, id + "F3", {"entities" : qUnion([Q0]), "operationType" : NewBodyOperationType.REMOVE, "oppositeDirection" : true, "depth" : 25.4 * mm});
        }
    });
